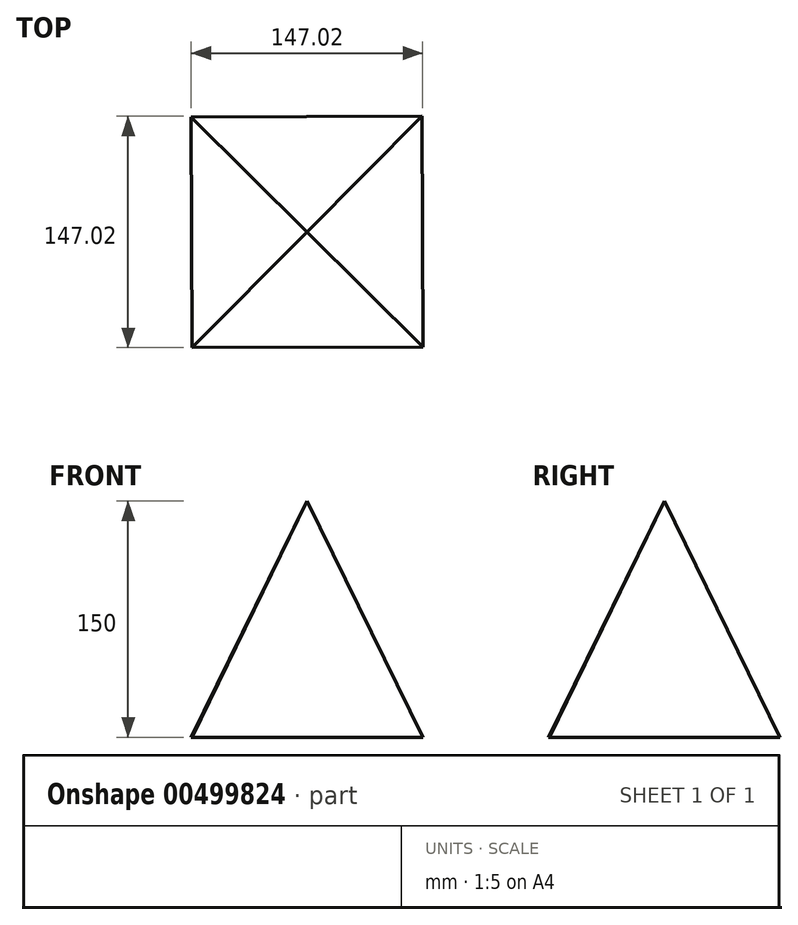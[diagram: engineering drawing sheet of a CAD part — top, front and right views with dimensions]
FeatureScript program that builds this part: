
annotation { "Feature Type Name" : "Feature", "Feature Type Description" : "" }
export const myFeature = defineFeature(function(context is Context, id is Id, definition is map)
    precondition{}
    {
        {
            var Q0;
            Q0=qCreatedBy(makeId("Top.planeOp"),FACE);
            var sketch = newSketch(context, id + "F0", { "sketchPlane" : qUnion([Q0])});
            skCircle(sketch, "E0.cCircle", {"center": v(0, 0) * mm, "radius": 103.61 * mm, "construction": true});
            skLineSegment(sketch, "E0.0", {"start": v(73.01, 73.51) * mm, "end": v(73.51, -73.01) * mm});
            skLineSegment(sketch, "E0.1", {"start": v(73.51, -73.01) * mm, "end": v(-73.01, -73.51) * mm});
            skLineSegment(sketch, "E0.2", {"start": v(-73.01, -73.51) * mm, "end": v(-73.51, 73.01) * mm});
            skLineSegment(sketch, "E0.3", {"start": v(-73.51, 73.01) * mm, "end": v(73.01, 73.51) * mm});
            skSolve(sketch);
        }
        {
            var Q0;
            Q0=qCreatedBy(makeId("Top.planeOp"),FACE);
            cPlane(context, id + "F1", {"entities" : qUnion([Q0]), "cplaneType" : CPlaneType.OFFSET, "offset" : 150 * mm, "width" : 150 * mm, "height" : 150 * mm});
        }
        {
            var Q0;
            Q0=qCreatedBy(id+"F1.planeOp",FACE);
            var sketch = newSketch(context, id + "F2", { "sketchPlane" : qUnion([Q0])});
            skPoint(sketch, "E1", {"position": v(0, 0) * mm});
            skSolve(sketch);
        }
        {
            var Q0;
            Q0=sQuery(id+"F2.wireOp",VERTEX,"E1");
            var Q1;
            Q1=makeQuery(id+"F0.imprint","IMPRINT",FACE,{"disambiguationData":[TD([[makeQuery(id+"F0.imprint","IMPRINT",EDGE,{"derivedFrom":sQuery(id+"F0.wireOp",EDGE,"E0.0")}),-1.0]])]});
            loft(context, id + "F3", {"sheetProfilesArray" : [{ "sheetProfileEntities" : qUnion([Q0]) }, { "sheetProfileEntities" : qUnion([Q1]) }]});
        }
    });
